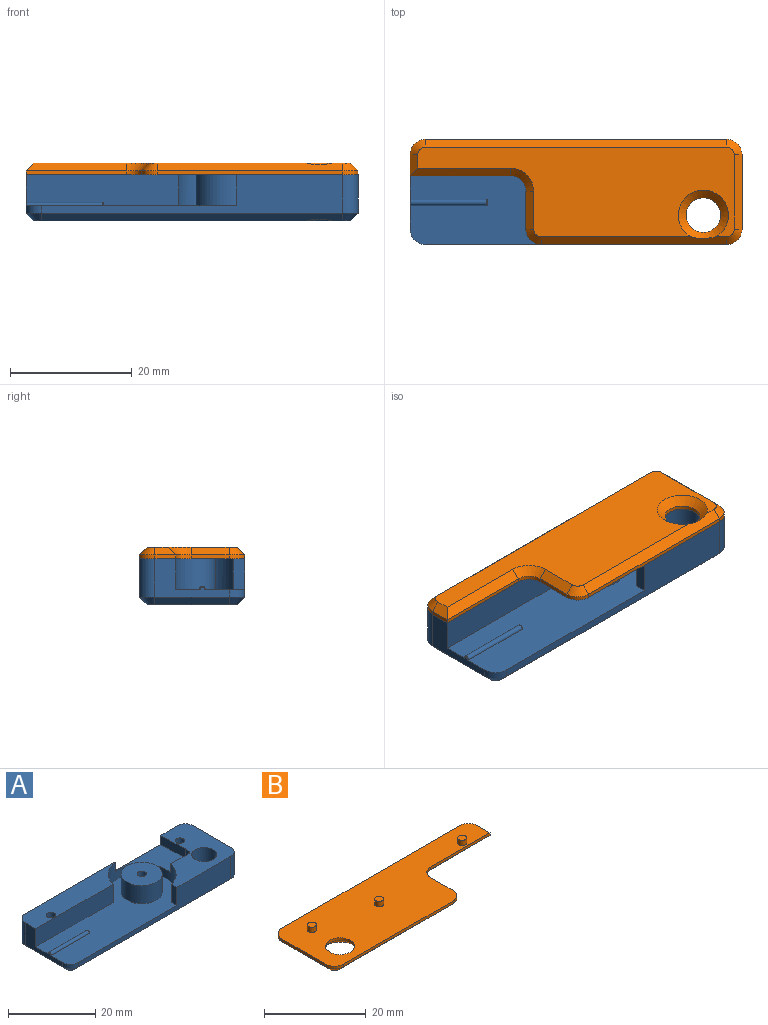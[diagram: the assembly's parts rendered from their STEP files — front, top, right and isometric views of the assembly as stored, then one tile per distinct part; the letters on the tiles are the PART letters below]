
ASSEMBLY  parts=2 mates=1
PART A: 43 faces, bbox 54.6x17.3x7.6 mm
  f0: plane 40.42x17.14mm, normal (0,0,1), area 415.8mm2, adj f1,f2,f3,f15,f16,f20,f24,f39
  f1: plane 12.19x6.35mm, normal (-1,0,0), area 33.2mm2, adj f0,f2,f8,f24,f27,f34,f41
  f2: cylinder r=2.54mm len=2.54mm, axis (0,0,-1), area 5.1mm2, adj f0,f1,f3,f32
  f3: plane 49.5x6.35mm, normal (0,-1,0), area 151.8mm2, adj f0,f2,f4,f16,f18,f31
  f4: cylinder r=2.54mm len=6.35mm, axis (0,0,-1), area 25.3mm2, adj f3,f5,f18,f33
  f5: plane 12.19x6.35mm, normal (1,0,0), area 77.4mm2, adj f4,f6,f18,f35
  f6: cylinder r=2.54mm len=6.35mm, axis (0,0,-1), area 25.3mm2, adj f5,f7,f18,f37
  f7: plane 49.5x6.35mm, normal (0,1,0), area 276.2mm2, adj f6,f8,f11,f18,f25,f27,f29,f38
  f8: cylinder r=2.54mm len=6.35mm, axis (0,0,-1), area 25.3mm2, adj f1,f7,f27,f36
  f9: cylinder r=2.86mm len=6.35mm, axis (0,0,-1), area 114mm2, adj f18,f30
  f10: plane 52.04x14.73mm, normal (0,0,-1), area 713.4mm2, adj f30,f31,f32,f33,f34,f35,f36,f37
  f11: plane 7.73x2.54mm, normal (-1,-0.03,0), area 19.6mm2, adj f7,f12,f18,f29
  f12: plane 2.54x1.27mm, normal (-1,0,0), area 3.2mm2, adj f11,f13,f18,f29
  f13: cylinder r=0.64mm len=2.54mm, axis (0,0,-1), area 2.5mm2, adj f12,f14,f18,f29
  f14: plane 5.91x2.54mm, normal (0,1,0), area 15mm2, adj f13,f15,f18,f29
  f15: cylinder r=7.78mm len=15.32mm, axis (0,0,-1), area 128.3mm2, adj f0,f14,f16,f18,f24,f25,f27,f29
  f16: plane 5.08x1.82mm, normal (-1,0,0), area 9.3mm2, adj f0,f3,f15,f18
  f17: cylinder r=1.08mm len=5.08mm, axis (0,0,-1), area 34.5mm2, adj f18,f19
  f18: plane 20.04x17.27mm, normal (0,0,1), area 174.3mm2, adj f3,f4,f5,f6,f7,f9,f11,f12
  f19: plane 2.16x2.16mm, normal (0,0,1), area 3.7mm2, adj f17
  f20: cylinder r=4.7mm len=9.4mm, axis (0,0,-1), area 150mm2, adj f0,f22
  f21: cylinder r=1.08mm len=5.08mm, axis (0,0,-1), area 34.5mm2, adj f22,f23
  f22: plane 9.4x9.4mm, normal (0,0,1), area 65.7mm2, adj f20,f21
  f23: plane 2.16x2.16mm, normal (0,0,1), area 3.7mm2, adj f21
  f24: plane 25.1x5.08mm, normal (0,-1,0), area 127.5mm2, adj f0,f1,f15,f27
  f25: plane 2.54x0.21mm, normal (1,0,0), area 0.5mm2, adj f7,f15,f27,f29
  f26: cylinder r=1.08mm len=5.08mm, axis (0,0,-1), area 34.5mm2, adj f27,f28
  f27: plane 31.56x5.98mm, normal (0,0,1), area 157.3mm2, adj f1,f7,f8,f15,f24,f25,f26
  f28: plane 2.16x2.16mm, normal (0,0,1), area 3.7mm2, adj f26
  f29: plane 15.21x9.64mm, normal (0,0,1), area 74.6mm2, adj f7,f11,f12,f13,f14,f15,f25
  f30: cone r=4.13mm half-angle=45deg, axis (0,0,-1), area 38.3mm2, adj f9,f10,f31
  f31: plane 49.5x1.27mm, normal (0,-0.71,-0.71), area 87.8mm2, adj f3,f10,f30,f32,f33
  f32: cone r=2.54mm half-angle=45deg, axis (0,0,1), area 5.4mm2, adj f2,f10,f31,f34
  f33: cone r=2.54mm half-angle=45deg, axis (0,0,1), area 5.4mm2, adj f4,f10,f31,f35
  f34: plane 12.19x1.27mm, normal (-0.71,0,-0.71), area 21.9mm2, adj f1,f10,f32,f36
  f35: plane 12.19x1.27mm, normal (0.71,0,-0.71), area 21.9mm2, adj f5,f10,f33,f37
  f36: cone r=2.54mm half-angle=45deg, axis (0,0,1), area 5.4mm2, adj f8,f10,f34,f38
  f37: cone r=2.54mm half-angle=45deg, axis (0,0,1), area 5.4mm2, adj f6,f10,f35,f38
  f38: plane 49.5x1.27mm, normal (0,0.71,-0.71), area 88.9mm2, adj f7,f10,f36,f37
  f39: cylinder r=0.51mm len=12.45mm, axis (-1,0,0), area 19.9mm2, adj f0,f41,f42
  f40: plane 0.76x0.38mm, normal (1,0,0), area 0.2mm2, adj f0,f42
  f41: torus R=0.38mm, axis (1,0,0), area 0.3mm2, adj f0,f1,f39
  f42: torus R=0.38mm, axis (-1,0,0), area 0.3mm2, adj f0,f39,f40
PART B: 32 faces, bbox 54.6x17.3x3.2 mm
  f0: plane 3.43x0.64mm, normal (1,0,0), area 2.2mm2, adj f1,f11,f12,f20
  f1: cylinder r=2.54mm len=2.54mm, axis (0,0,-1), area 2.5mm2, adj f0,f2,f12,f22
  f2: plane 49.5x0.64mm, normal (0,1,0), area 31.4mm2, adj f1,f3,f12,f24
  f3: cylinder r=2.54mm len=2.54mm, axis (0,0,-1), area 2.5mm2, adj f2,f4,f12,f26
  f4: plane 12.19x0.64mm, normal (-1,0,0), area 7.7mm2, adj f3,f5,f12,f29
  f5: cylinder r=2.54mm len=2.54mm, axis (0,0,-1), area 2.5mm2, adj f4,f6,f12,f31
  f6: plane 30.45x0.64mm, normal (0,-1,0), area 19.3mm2, adj f5,f7,f12,f30
  f7: cylinder r=2.54mm len=2.54mm, axis (0,0,-1), area 2.5mm2, adj f6,f8,f12,f27
  f8: plane 6.22x0.64mm, normal (1,0,0), area 4mm2, adj f7,f9,f12,f25
  f9: cylinder r=2.54mm len=2.54mm, axis (0,0,-1), area 2.5mm2, adj f8,f11,f12,f23
  f10: cylinder r=2.86mm len=5.72mm, axis (0,0,-1), area 11.4mm2, adj f12,f28
  f11: plane 16.51x0.64mm, normal (0,-1,0), area 10.5mm2, adj f0,f9,f12,f21
  f12: plane 54.58x17.27mm, normal (0,0,1), area 690.2mm2, adj f0,f1,f2,f3,f4,f5,f6,f7
  f13: plane 52.04x14.73mm, normal (0,0,-1), area 501.2mm2, adj f20,f21,f22,f23,f24,f25,f26,f27
  f14: cylinder r=0.89mm len=1.78mm, axis (0,0,-1), area 7.1mm2, adj f12,f15
  f15: plane 1.78x1.78mm, normal (0,0,1), area 2.5mm2, adj f14
  f16: cylinder r=0.89mm len=1.78mm, axis (0,0,-1), area 7.1mm2, adj f12,f17
  f17: plane 1.78x1.78mm, normal (0,0,1), area 2.5mm2, adj f16
  f18: cylinder r=0.89mm len=1.78mm, axis (0,0,-1), area 7.1mm2, adj f12,f19
  f19: plane 1.78x1.78mm, normal (0,0,1), area 2.5mm2, adj f18
  f20: plane 3.43x1.27mm, normal (0.71,0,-0.71), area 5mm2, adj f0,f13,f21,f22
  f21: plane 16.51x1.27mm, normal (0,-0.71,-0.71), area 28.5mm2, adj f11,f13,f20,f23
  f22: cone r=2.54mm half-angle=45deg, axis (0,0,1), area 5.4mm2, adj f1,f13,f20,f24
  f23: cone r=3.81mm half-angle=45deg, axis (0,0,-1), area 9mm2, adj f9,f13,f21,f25
  f24: plane 49.5x1.27mm, normal (0,0.71,-0.71), area 88.9mm2, adj f2,f13,f22,f26
  f25: plane 6.22x1.27mm, normal (0.71,0,-0.71), area 11.2mm2, adj f8,f13,f23,f27
  f26: cone r=2.54mm half-angle=45deg, axis (0,0,1), area 5.4mm2, adj f3,f13,f24,f29
  f27: cone r=2.54mm half-angle=45deg, axis (0,0,1), area 5.4mm2, adj f7,f13,f25,f30
  f28: cone r=4.13mm half-angle=45deg, axis (0,0,-1), area 38.3mm2, adj f10,f13,f30
  f29: plane 12.19x1.27mm, normal (-0.71,0,-0.71), area 21.9mm2, adj f4,f13,f26,f31
  f30: plane 30.45x1.27mm, normal (0,-0.71,-0.71), area 53.6mm2, adj f6,f13,f27,f28,f31
  f31: cone r=2.54mm half-angle=45deg, axis (0,0,1), area 5.4mm2, adj f5,f13,f29,f30
PLACE A t=(-18.59,-6.19,2.57)mm
PLACE B rot(axis=(0,1,0),180deg) t=(-46.8,-7.08,12.1)mm
MATE fastened B.f14 <-> A.f17  axis (0,0,-1) through (-25.86,-3.01,8.92)mm
